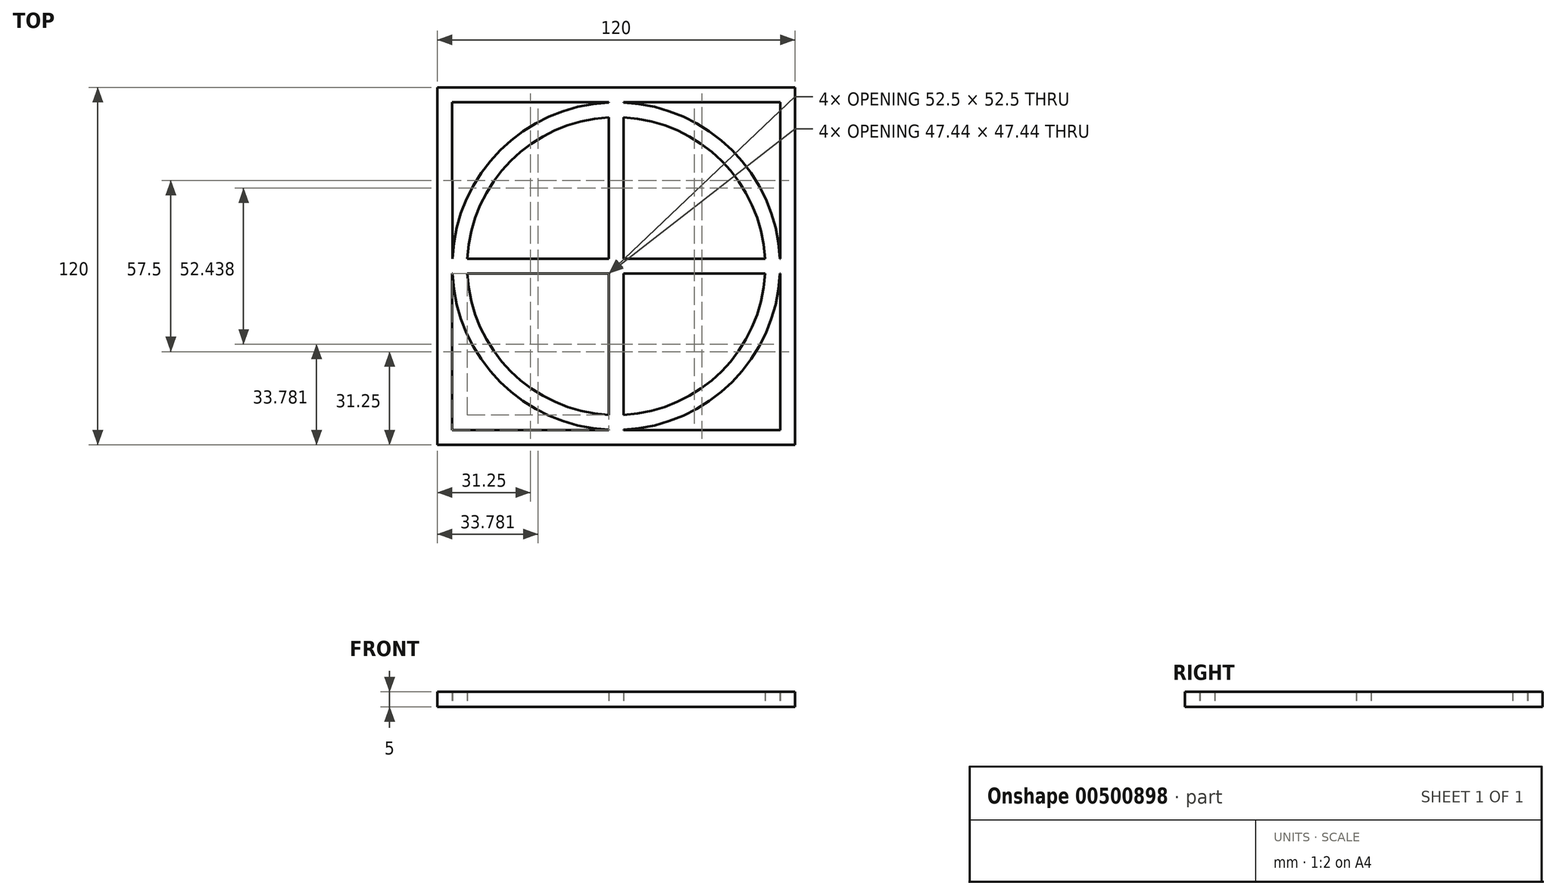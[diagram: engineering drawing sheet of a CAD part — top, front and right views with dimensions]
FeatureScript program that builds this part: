
annotation { "Feature Type Name" : "Feature", "Feature Type Description" : "" }
export const myFeature = defineFeature(function(context is Context, id is Id, definition is map)
    precondition{}
    {
        {
            var Q0;
            Q0=qCreatedBy(makeId("Top.planeOp"),FACE);
            var sketch = newSketch(context, id + "F0", { "sketchPlane" : qUnion([Q0])});
            skArc(sketch, "E0", {"start": v(49.94, 2.5) * mm, "mid": v(35.36, 35.36) * mm, "end": v(2.5, 49.94) * mm});
            skArc(sketch, "E1.0", {"start": v(-2.5, 54.94) * mm, "mid": v(-38.9, 38.9) * mm, "end": v(-54.94, 2.5) * mm});
            skLineSegment(sketch, "E2.bottom", {"start": v(-55, -55) * mm, "end": v(55, -55) * mm});
            skLineSegment(sketch, "E2.top", {"start": v(-55, 55) * mm, "end": v(-2.5, 55) * mm});
            skLineSegment(sketch, "E2.left", {"start": v(-55, -55) * mm, "end": v(-55, -2.5) * mm});
            skLineSegment(sketch, "E2.right", {"start": v(55, -55) * mm, "end": v(55, -2.5) * mm});
            skLineSegment(sketch, "E3.0", {"start": v(-60, -60) * mm, "end": v(-60, 60) * mm});
            skLineSegment(sketch, "E3.1", {"start": v(-60, -60) * mm, "end": v(60, -60) * mm});
            skLineSegment(sketch, "E3.2", {"start": v(60, -60) * mm, "end": v(60, 60) * mm});
            skLineSegment(sketch, "E3.3", {"start": v(-60, 60) * mm, "end": v(60, 60) * mm});
            skLineSegment(sketch, "E4", {"start": v(-60, 0) * mm, "end": v(60, 0) * mm, "construction": true});
            skLineSegment(sketch, "E5", {"start": v(0, 60) * mm, "end": v(0, -60) * mm, "construction": true});
            skLineSegment(sketch, "E6.0", {"start": v(-55, -2.5) * mm, "end": v(-54.94, -2.5) * mm});
            skLineSegment(sketch, "E7.0", {"start": v(-49.94, 2.5) * mm, "end": v(-2.5, 2.5) * mm});
            skLineSegment(sketch, "E8.0", {"start": v(-2.5, 55) * mm, "end": v(-2.5, 54.94) * mm});
            skLineSegment(sketch, "E9.0", {"start": v(2.5, 55) * mm, "end": v(2.5, 54.94) * mm});
            skLineSegment(sketch, "E10.trimOffspring", {"start": v(2.5, 55) * mm, "end": v(55, 55) * mm});
            skArc(sketch, "E11.trimOffspring", {"start": v(54.94, 2.5) * mm, "mid": v(38.9, 38.9) * mm, "end": v(2.5, 54.94) * mm});
            skLineSegment(sketch, "E12.trimOffspring", {"start": v(55, 2.5) * mm, "end": v(55, 55) * mm});
            skLineSegment(sketch, "E13.trimOffspring", {"start": v(54.94, -2.5) * mm, "end": v(55, -2.5) * mm});
            skLineSegment(sketch, "E14.trimOffspring", {"start": v(54.94, 2.5) * mm, "end": v(55, 2.5) * mm});
            skLineSegment(sketch, "E15.trimOffspring", {"start": v(2.5, -54.94) * mm, "end": v(2.5, -55) * mm});
            skArc(sketch, "E16.trimOffspring", {"start": v(2.5, -54.94) * mm, "mid": v(38.9, -38.9) * mm, "end": v(54.94, -2.5) * mm});
            skLineSegment(sketch, "E17.trimOffspring", {"start": v(-2.5, -54.94) * mm, "end": v(-2.5, -55) * mm});
            skArc(sketch, "E18.trimOffspring", {"start": v(2.5, -49.94) * mm, "mid": v(35.36, -35.36) * mm, "end": v(49.94, -2.5) * mm});
            skArc(sketch, "E19.trimOffspring", {"start": v(-54.94, -2.5) * mm, "mid": v(-38.9, -38.9) * mm, "end": v(-2.5, -54.94) * mm});
            skLineSegment(sketch, "E20.trimOffspring", {"start": v(-49.94, -2.5) * mm, "end": v(-2.5, -2.5) * mm});
            skArc(sketch, "E21.trimOffspring", {"start": v(-49.94, -2.5) * mm, "mid": v(-35.36, -35.36) * mm, "end": v(-2.5, -49.94) * mm});
            skLineSegment(sketch, "E22.trimOffspring", {"start": v(-2.5, 49.94) * mm, "end": v(-2.5, 2.5) * mm});
            skLineSegment(sketch, "E23.trimOffspring", {"start": v(2.5, 49.94) * mm, "end": v(2.5, 2.5) * mm});
            skArc(sketch, "E24.trimOffspring", {"start": v(-2.5, 49.94) * mm, "mid": v(-35.36, 35.36) * mm, "end": v(-49.94, 2.5) * mm});
            skLineSegment(sketch, "E25.trimOffspring", {"start": v(2.5, -2.5) * mm, "end": v(2.5, -49.94) * mm});
            skLineSegment(sketch, "E26.trimOffspring", {"start": v(2.5, -2.5) * mm, "end": v(49.94, -2.5) * mm});
            skLineSegment(sketch, "E27.trimOffspring", {"start": v(-2.5, -2.5) * mm, "end": v(-2.5, -49.94) * mm});
            skLineSegment(sketch, "E28.trimOffspring", {"start": v(2.5, 2.5) * mm, "end": v(49.94, 2.5) * mm});
            skLineSegment(sketch, "E29", {"start": v(-55, 55) * mm, "end": v(-54.94, 2.5) * mm});
            skSolve(sketch);
        }
        {
            var Q0;
            Q0=makeQuery(id+"F0.imprint","IMPRINT",FACE,{"disambiguationData":[TD([[makeQuery(id+"F0.imprint","IMPRINT",EDGE,{"derivedFrom":sQuery(id+"F0.wireOp",EDGE,"E0")}),-1.0]])]});
            extrude(context, id + "F1", {"entities" : qUnion([Q0]), "depth" : 5 * mm});
        }
    });
